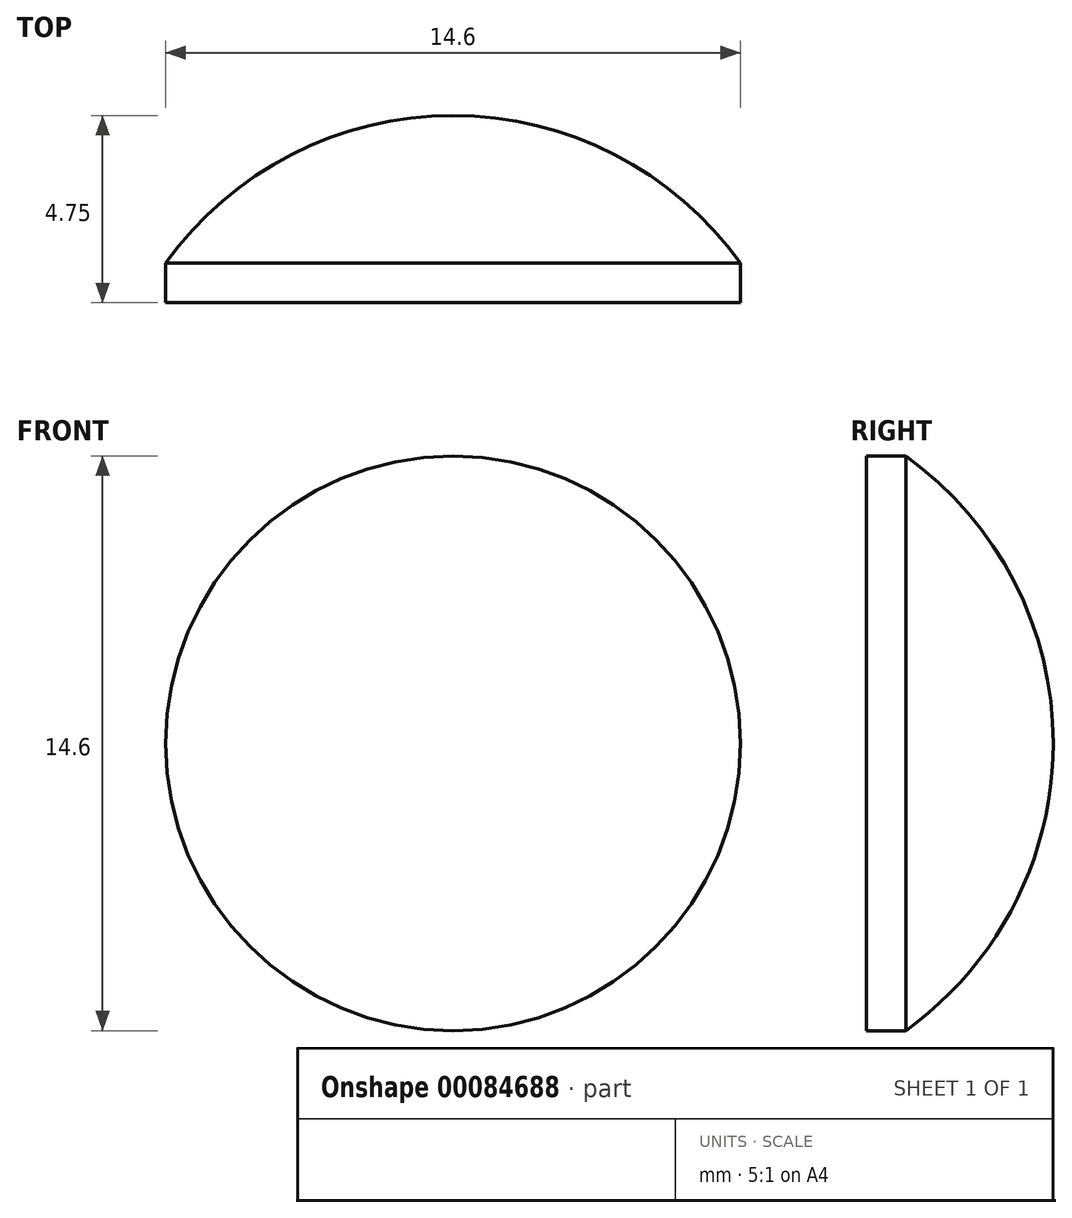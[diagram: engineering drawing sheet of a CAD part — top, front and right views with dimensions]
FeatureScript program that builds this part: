
annotation { "Feature Type Name" : "Feature", "Feature Type Description" : "" }
export const myFeature = defineFeature(function(context is Context, id is Id, definition is map)
    precondition{}
    {
        {
            var Q0;
            Q0=qCreatedBy(makeId("Right.planeOp"),FACE);
            var sketch = newSketch(context, id + "F0", { "sketchPlane" : qUnion([Q0])});
            skLineSegment(sketch, "E0", {"start": v(0, 0) * mm, "end": v(3.75, 0) * mm});
            skArc(sketch, "E1", {"start": v(0, -7.3) * mm, "mid": v(2.76, -4.1) * mm, "end": v(3.75, 0) * mm});
            skLineSegment(sketch, "E2", {"start": v(0, 0) * mm, "end": v(-1, 0) * mm});
            skLineSegment(sketch, "E3", {"start": v(-1, 0) * mm, "end": v(-1, -7.3) * mm});
            skLineSegment(sketch, "E4", {"start": v(-1, -7.3) * mm, "end": v(0, -7.3) * mm});
            skSolve(sketch);
        }
        {
            var Q0;
            Q0=makeQuery(id+"F0.imprint","IMPRINT",FACE,{"disambiguationData":[TD([[makeQuery(id+"F0.imprint","IMPRINT",EDGE,{"derivedFrom":sQuery(id+"F0.wireOp",EDGE,"be1pb1mZ-hwWR-6vms-K4jB-lGV09oohTnY4")}),1.0]])]});
            var Q1;
            Q1=makeQuery(id+"F0.imprint","IMPRINT",FACE,{"disambiguationData":[TD([[makeQuery(id+"F0.imprint","IMPRINT",EDGE,{"derivedFrom":sQuery(id+"F0.wireOp",EDGE,"E0")}),-1.0]])]});
            var Q2;
            Q2=makeQuery(id+"F0.imprint","IMPRINT",FACE,{"disambiguationData":[TD([[makeQuery(id+"F0.imprint","IMPRINT",EDGE,{"derivedFrom":sQuery(id+"F0.wireOp",EDGE,"3LW488qJ-SEb6-bsuS-C0Jy-NbQtP4rW3xZo.bottom")}),-1.0]])]});
            var Q3;
            Q3=sQuery(id+"F0.wireOp",EDGE,"E0");
            revolve(context, id + "F1", {"entities" : qUnion([Q0, Q1, Q2]), "axis" : qUnion([Q3]), "revolveType" : RevolveType.FULL});
        }
    });
